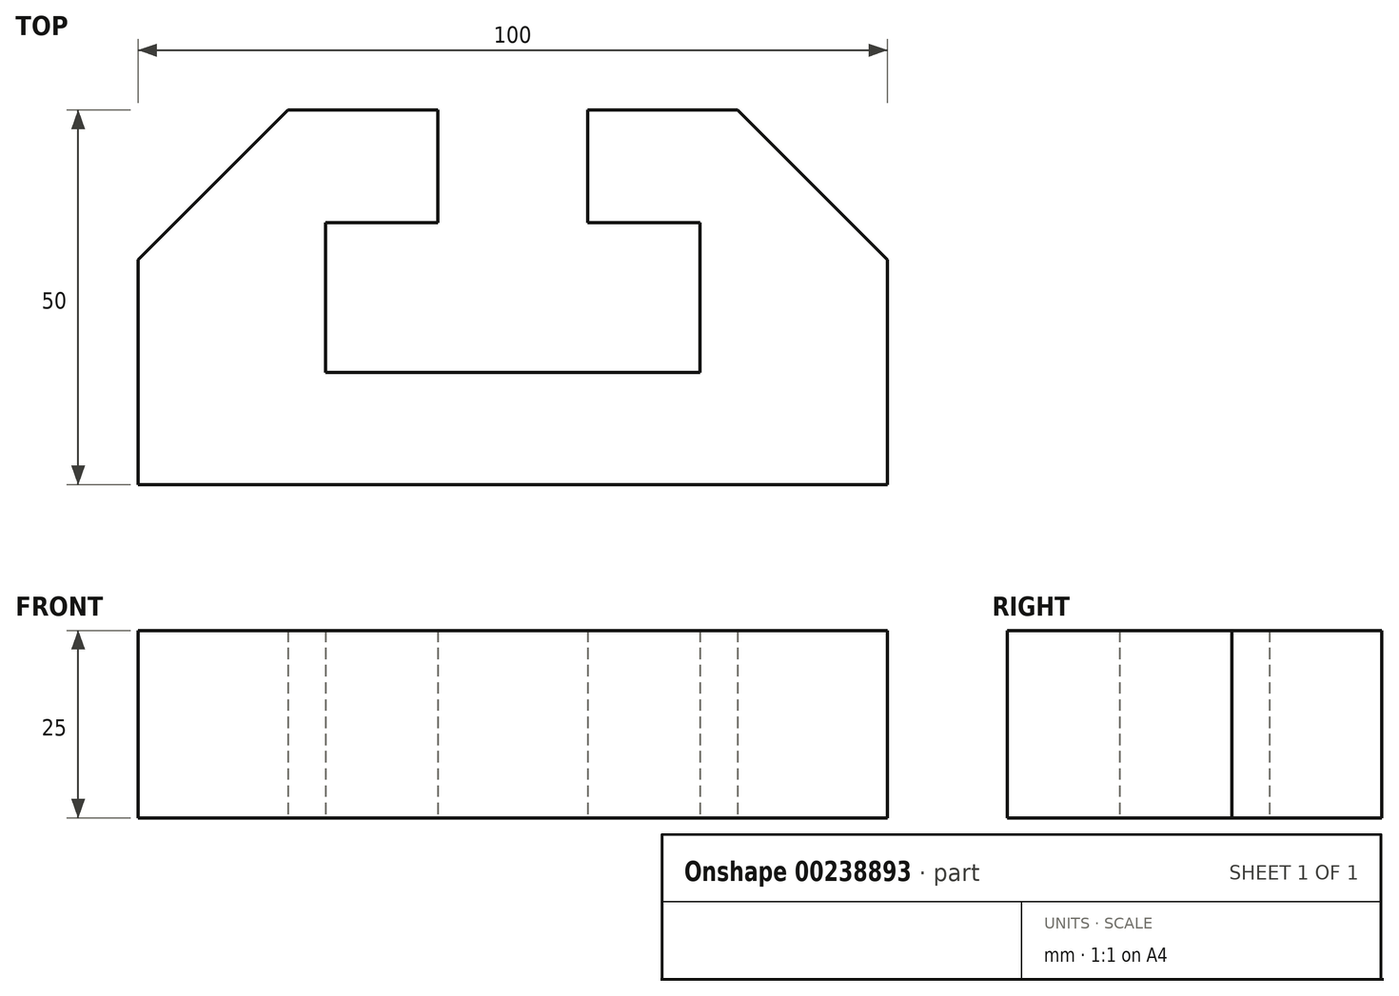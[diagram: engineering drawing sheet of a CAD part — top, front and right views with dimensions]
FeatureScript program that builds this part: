
annotation { "Feature Type Name" : "Feature", "Feature Type Description" : "" }
export const myFeature = defineFeature(function(context is Context, id is Id, definition is map)
    precondition{}
    {
        {
            var Q0;
            Q0=qCreatedBy(makeId("Top.planeOp"),FACE);
            var sketch = newSketch(context, id + "F0", { "sketchPlane" : qUnion([Q0])});
            skLineSegment(sketch, "E0", {"start": v(-60, -66.14) * mm, "end": v(40, -66.14) * mm});
            skLineSegment(sketch, "E1", {"start": v(-60, -66.14) * mm, "end": v(-60, -36.14) * mm});
            skLineSegment(sketch, "E2", {"start": v(40, -66.14) * mm, "end": v(40, -36.14) * mm});
            skLineSegment(sketch, "E3", {"start": v(-60, -36.14) * mm, "end": v(-40, -16.14) * mm});
            skLineSegment(sketch, "E4", {"start": v(-40, -16.14) * mm, "end": v(-20, -16.14) * mm});
            skLineSegment(sketch, "E5", {"start": v(-20, -16.14) * mm, "end": v(-20, -31.14) * mm});
            skLineSegment(sketch, "E6", {"start": v(-20, -31.14) * mm, "end": v(-35, -31.14) * mm});
            skLineSegment(sketch, "E7", {"start": v(-35, -31.14) * mm, "end": v(-35, -51.14) * mm});
            skLineSegment(sketch, "E8", {"start": v(-35, -51.14) * mm, "end": v(15, -51.14) * mm});
            skLineSegment(sketch, "E9", {"start": v(15, -51.14) * mm, "end": v(15, -31.14) * mm});
            skLineSegment(sketch, "E10", {"start": v(15, -31.14) * mm, "end": v(0, -31.14) * mm});
            skLineSegment(sketch, "E11", {"start": v(0, -31.14) * mm, "end": v(0, -16.14) * mm});
            skLineSegment(sketch, "E12", {"start": v(0, -16.14) * mm, "end": v(20, -16.14) * mm});
            skLineSegment(sketch, "E13", {"start": v(20, -16.14) * mm, "end": v(40, -36.14) * mm});
            skSolve(sketch);
        }
        {
            var Q0;
            Q0=makeQuery(id+"F0.imprint","IMPRINT",FACE,{"disambiguationData":[TD([[makeQuery(id+"F0.imprint","IMPRINT",EDGE,{"derivedFrom":sQuery(id+"F0.wireOp",EDGE,"E0")}),1.0]])]});
            extrude(context, id + "F1", {"entities" : qUnion([Q0]), "depth" : 25 * mm});
        }
    });
